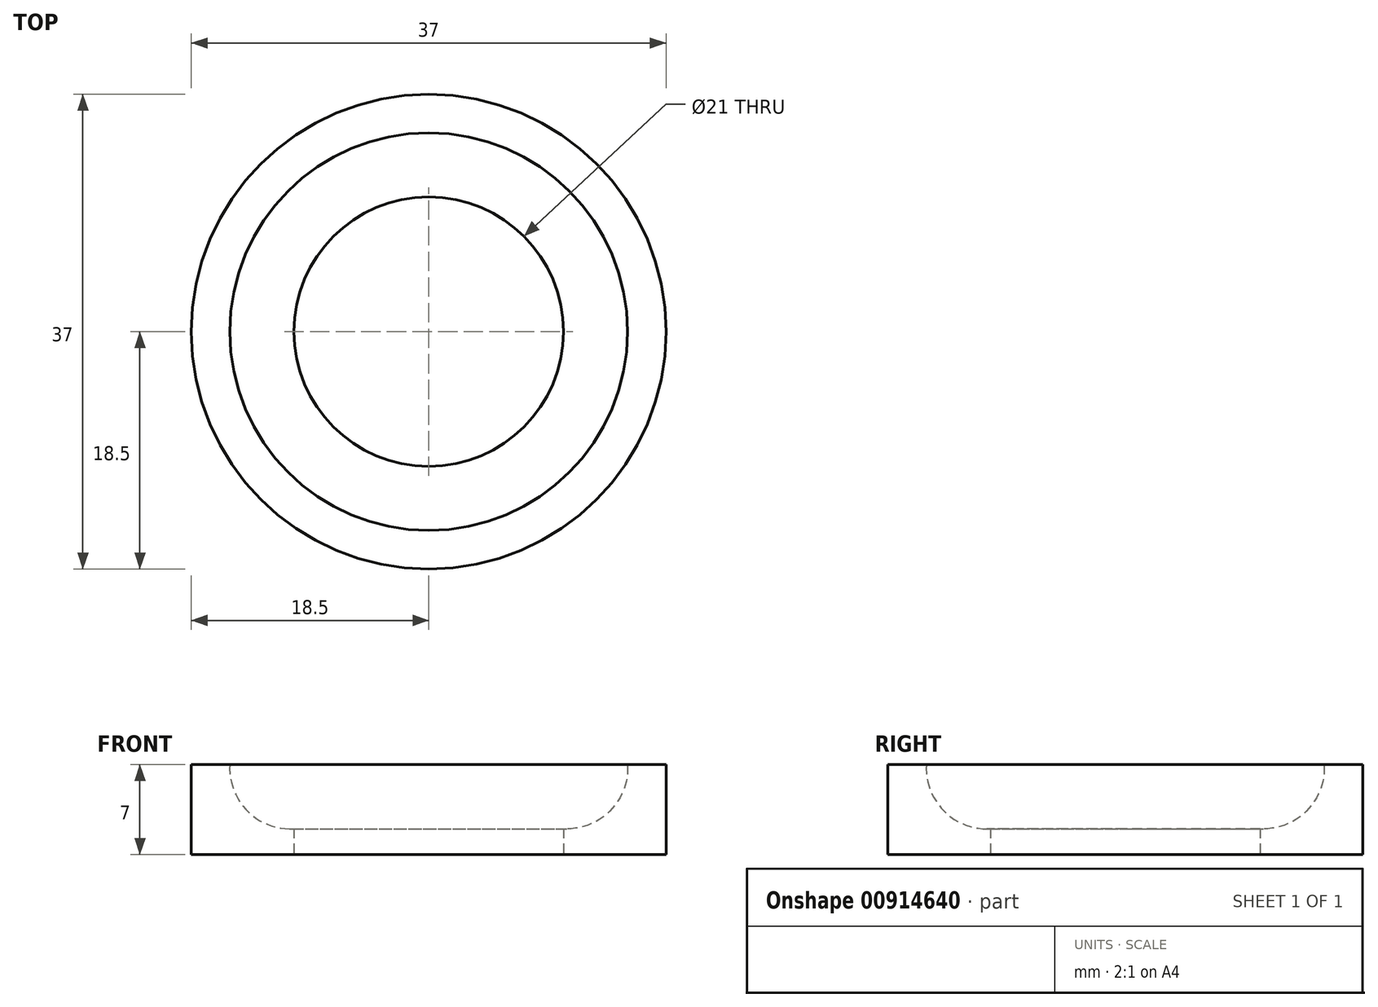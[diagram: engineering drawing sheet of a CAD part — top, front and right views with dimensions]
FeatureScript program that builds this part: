
annotation { "Feature Type Name" : "Feature", "Feature Type Description" : "" }
export const myFeature = defineFeature(function(context is Context, id is Id, definition is map)
    precondition{}
    {
        {
            var Q0;
            Q0=qCreatedBy(makeId("Front.planeOp"),FACE);
            var sketch = newSketch(context, id + "F0", { "sketchPlane" : qUnion([Q0])});
            skLineSegment(sketch, "E0", {"start": v(0, 0) * mm, "end": v(0, 50) * mm, "construction": true});
            skLineSegment(sketch, "E1", {"start": v(10.5, 0) * mm, "end": v(10.5, 2) * mm});
            skLineSegment(sketch, "E2", {"start": v(10.5, 2) * mm, "end": v(10.5, 7) * mm, "construction": true});
            skLineSegment(sketch, "E3", {"start": v(15.5, 7) * mm, "end": v(10.5, 7) * mm, "construction": true});
            skLineSegment(sketch, "E4", {"start": v(15.5, 7) * mm, "end": v(18.5, 7) * mm});
            skLineSegment(sketch, "E5", {"start": v(18.5, 7) * mm, "end": v(18.5, 0) * mm});
            skLineSegment(sketch, "E6", {"start": v(18.5, 0) * mm, "end": v(10.5, 0) * mm});
            skArc(sketch, "E7", {"start": v(10.5, 2) * mm, "mid": v(14.12, 3.38) * mm, "end": v(15.5, 7) * mm});
            skSolve(sketch);
        }
        {
            var Q0;
            Q0=qSketchRegion(id+"F0",true);
            var Q1;
            Q1=sQuery(id+"F0.wireOp",EDGE,"E0");
            revolve(context, id + "F1", {"surfaceOperationType" : NewSurfaceOperationType.NEW, "entities" : qUnion([Q0]), "axis" : qUnion([Q1]), "revolveType" : RevolveType.FULL});
        }
    });
